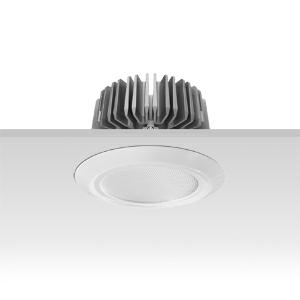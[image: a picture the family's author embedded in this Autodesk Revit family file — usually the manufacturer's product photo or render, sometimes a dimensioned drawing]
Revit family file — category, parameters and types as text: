
# Revit family: 3f_filippi_-_3f_reno_bianco_ampio_3f_filippi_-_30387_a01035_-_3f_reno_150_wh_3000-930_dali_wide___vs_wh_c1a0
name_source: partatom
category: Lighting Fixtures
units: mm (PartAtom-declared; Revit-internal decimal feet)

## family parameters
Cut with Voids When Loaded = No
Host = Face
Light Source = No
Part Type = Normal
Room Calculation Point = No
Round Connector Dimension = Use Diameter
Shared = No

## types (1)
- 3F Filippi - 3F Reno Bianco Ampio (1 x LED, 2301 lm, 37 W, 3000 K)
    Apparent Load = 37 VA
    Approval mark = CE
    CIE Flux Codes = 74 93 99 100 100
    Color Rendering = 90
    Color Temperature = 3000 K
    Control Gear = Electronic transformer
    Default Elevation = 1800 mm
    Description = ILLUMINOTECHNICAL
Luminous efficiency 100% (DLOR 100%, ULOR 0%).
Initial luminous flux of the luminaire 2301 lm.
Direct symmetric wide distribution.
Installation Interdistance Transv.D = 1.12 x hu - Long.D = 1.11 x hu.
Tabular UGR (CIE 117 - 4H-8H; S=0.25H; 70/50/20): RUG 23.9 - 23.7.
Beam angle: 74° - 73°.
Luminous efficacy 62 lm/W.
Lifetime (L90/B10): 30000 h. (tq+25°C)
Lifetime (L85/B10): 50000 h. (tq+25°C)
Lifetime (L70/B10): 80000 h. (tq+25°C)
Sudden decreased luminous flux after 50000 hours: 0% (C0).
Photobiological safety in compliance with IEC/TR 62778: RG0 risk exempt, (IEC 62471).
In compliance with IEC/EN 62722-2-1 - IEC/EN 62717 standards.

SOURCE
Compact LED module 3000/930.
Energy efficiency class (UE 2019/2020 - UE 2019/2015): F.
CIE 13.3 Colour rendering index: CRI >90 (R9 >50%).
IES TM-30 Fidelity Index: Rf = 92 Rg = 101.
CCT nominal colour temperature 3000 K.
Colour initial tolerance (MacAdam): SDCM 3.
Zhaga Book 3 compliant.

MECHANICAL
Passive heat dissipator in die-casting aluminium, oversized, for optimum thermal management of the LED module.
Parabolic element with graduated/concentric rings in white polycarbonate.
Transparent external lens with glossy and satin differentiated surfaces, with a cooling and anti-insect system in methacrylate (PMMA).
Fastening spring clips in stainless steel.
Dimensions: diameter 176 mm, height 111 mm. Weight 1.55 kg.
IP44 protection degree for exposed part, IP20 for recessed part.
Mechanical strength to impacts IK06 (1 joule).
Glow-wire test resistance 650°C.

ELECTRICAL
Wiring on a separate unit.
Halogen Free DALI-2 DATI (Parts 251, 252, 253), PUSH-DIM, electronic wiring 230V-50/60Hz, power factor 0.97 at full load, THD <25%, constant output current, SELV, class II, 1 driver, 1 DALI addresse.
Power of the luminaire 37 W.
ENEC - CE.
SAFE FLICKER: PstLM=<1 and SVM=<0.4 (IEC TR 61547-1 and IEC TR 63158), to ensure a more comfortable and safe light.
Luminaire compliant with EN 60598-2-22 for power supply from a centralised emergency system CPSS (Central Power Supply System), not incorporated in the luminaire - high risk areas excluded. The default power and flux are 100% in AC and 100% in DC.
Ambient temperature from 0°C to +25°C.
Temperature class T6 max 85°C.
Relative humidity UR: <85%.

INSTALLATION
Pull-up recessed fitting.
False ceiling carving: 150 mm.
All accessories dedicated to this product are available on the Catalog and on our website www.3F-Filippi.com.

ACCESSORIES
A01035 - Anti-glare microprismatic VS moulded glass, tempered, not flammable, locked and in line with the trim, in white polycarbonate.

APPLICATIONS
Environments: architectural, commercial, exhibition areas, transit areas, corridors, shops, display windows, service areas.
In false ceilings with narrow voids.

LIGHT MANAGEMENT
Recommended minimum setting: 10%.
The luminaire, equipped with (DALI-2 DATI) driver, can be controlled manually with 3F Easy Dim technology or automatically/manually with wired or wireless DALI/D2D control systems.
The D2D driver guarantees interoperability with other devices with the same certification by making the following information available:
Device Data (Part 251), Energy Report (Part 252), Diagnosis & Maintenance (Part 253).
In electrical systems without a regulation system (manual or automatic) and DALI bus, a suitable jumper must be made on the DA-DA terminals of the appliance.

WARNING
Luminaire designed for disposal/recycling at end-of-life.
Replaceable (LED only) light source by a professional. Replaceable control gear by a professional.
    Height = 0 mm  [stored 0 ft]
    Lamp = 1 x LED
    Lamp Light Flux = 2301 lm
    Lamp Power = 37 W
    Lamp count = 1
    Length = 176 mm
    Lifetime = 50000 h
    Luminous efficacy = 62 lm/W
    Manufacturer = 3F Filippi
    ModVariant = No
    Model = 3F Filippi - 30387+A01035 - 3F Reno 150 WH 3000-930 DALI WIDE + VS WH
    Mounting Place = Ceiling
    Mounting Type = Recessed
    Number of Poles = 1
    OnlyDefault = Yes
    Power Factor = 1
    Product Name = 3F Filippi - 3F Reno Bianco Ampio
    Product group = recessed luminaire
    ProductGroupID = 4
    Protection Class = Protection class II
    Protection Degree = IP 20
    RLX_Detail_Level = 1
    RLX_Emergency_Light_Flux = 0 lm
    RLX_Emergency_Type = 0
    RLX_Emergency_Type_DB = No
    RlxData = <blob elided: 85365 chars, md5=53b459b5>
    Socket = socket
    Standby Power = 0 W
    System Light Flux = 2301 lm
    System Power = 37 W
    Type Comments = Product without accessories
    Type Image = 3ffilippi_3f_reno_150_wh_vs_smp.jpg
    URL = http://relux.com
    VarID = ---
    Voltage = 0 V
    Weight = 0.00 kg
    Width = 0 mm  [stored 0 ft]

note: [stored X ft] marks values corroborated as IEEE doubles in the binary element streams (Revit-internal decimal feet)

## geometry (parser evidence)
native form markers: Blend x4, Sweep x11
no freeform markers — native parametric forms only
